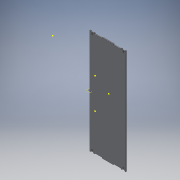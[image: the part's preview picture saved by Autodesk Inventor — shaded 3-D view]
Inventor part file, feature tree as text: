
AUTODESK INVENTOR PART (.ipt)
format: ipt  version: 2019 (Build 230136000, 136)  size: 308,224 bytes
history: native  units: in
note: dims shown in document units (in); Inventor stores cm internally (conversion verified against a paired STEP export)
features: reference x8, extrude x7, sketch x7, other x5, projected_geometry x4, fillet x2, plane x1, mirror x1, helix x1
ambient origin geometry x8: Origin, YZ Plane, XZ Plane, XY Plane, X Axis, Y Axis, Z Axis, Center Point
bodies: Solid1 (feature_tree)
feature tree (36):
  extrude  "Extrusion1"  Depth=0.1575in TaperAngle=0.0deg
  extrude  "Extrusion2"  Depth=0.1575in TaperAngle=0.0deg
  extrude  "Extrusion4"  Depth=2.5in
  extrude  "Extrusion5"  Depth=0.0394in
  plane  "Work Plane1"
  mirror  "Mirror1"
  sketch  "Sketch7"  dims[d15=1.5748in d16=10.0in d17=0.1575in d18=0.0in]
  extrude  "Extrusion6"  Depth=0.1575in
  fillet  "Fillet1"  Radius=0.1575in
  extrude  "Extrusion7"  Depth=0.1575in TaperAngle=0.0deg
  fillet  "Fillet2"  [1 undecoded]
  extrude  "Extrusion8"  [1 undecoded]
  sketch  "Sketch2"  dims[d0=7.874in d1=0.1575in d2=0.0in]
  sketch  "Sketch3"  dims[d3=0.1575in d4=0.0in d7=0.1575in d8=0.0in]
  reference  "Reference3"
  reference  "Reference4"
  sketch  "Sketch5"  dims[d9=0.1575in d10=0.0in d11=2.5in]
  projected_geometry  "Projected Loop1"
  projected_geometry  "Projected Loop2"
  projected_geometry  "Projected Loop3"
  projected_geometry  "Projected Loop4"
  sketch  "Sketch6"  dims[d12=0.1575in d13=0.0in d14=0.0394in]
  reference  "Reference7"
  reference  "Reference8"
  reference  "Reference9"
  sketch  "Sketch8"  dims[d19=0.7874in d20=0.1575in d21=0.0in]
  reference  "Reference10"
  sketch  "Sketch9"
  reference  "Reference11"
  reference  "Reference12"
  other  "<userpath>\Documents\CAD Files\Helix DLP\Helix DLP.iam"
  helix  "Helix DLP.iam"  [1 undecoded]
  other  "Maker_jigsaw_template:1"
  other  "Maker_jigsaw_template:2"
  other  "Projector:1"
  other  "Projector mount side:2"
note: 3 required parameter values undecoded (feature->parameter linkage not recoverable at this tier; creation-order binding heuristic only, values carry confidence <= 0.55)
